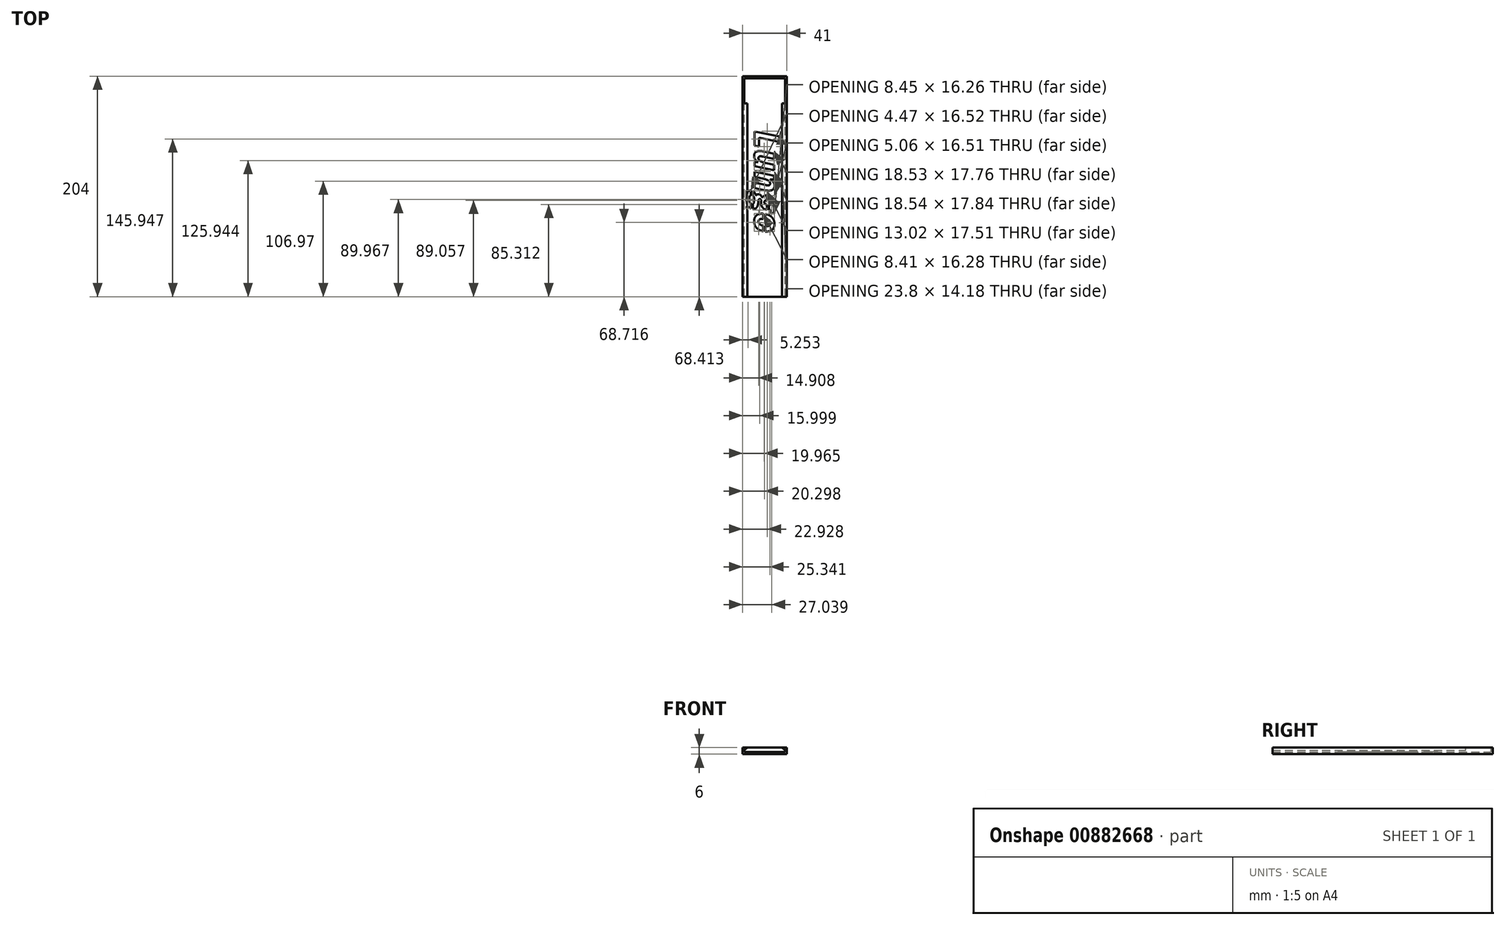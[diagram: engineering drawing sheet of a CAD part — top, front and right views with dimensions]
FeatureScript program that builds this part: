
annotation { "Feature Type Name" : "Feature", "Feature Type Description" : "" }
export const myFeature = defineFeature(function(context is Context, id is Id, definition is map)
    precondition{}
    {
        {
            var Q0;
            Q0=qCreatedBy(makeId("Front.planeOp"),FACE);
            var sketch = newSketch(context, id + "F0", { "sketchPlane" : qUnion([Q0])});
            skLineSegment(sketch, "E0", {"start": v(-20.5, 0) * mm, "end": v(20.5, 0) * mm});
            skLineSegment(sketch, "E1", {"start": v(20.5, 0) * mm, "end": v(20.5, 6) * mm});
            skLineSegment(sketch, "E2", {"start": v(20.5, 6) * mm, "end": v(16, 6) * mm});
            skLineSegment(sketch, "E3", {"start": v(19, 2) * mm, "end": v(-19, 2) * mm});
            skLineSegment(sketch, "E4", {"start": v(-16, 6) * mm, "end": v(-20.5, 6) * mm});
            skLineSegment(sketch, "E5", {"start": v(-20.5, 6) * mm, "end": v(-20.5, 0) * mm});
            skLineSegment(sketch, "E6", {"start": v(-16, 6) * mm, "end": v(16, 6) * mm});
            skLineSegment(sketch, "E7", {"start": v(16, 6) * mm, "end": v(19, 3.6) * mm});
            skLineSegment(sketch, "E8", {"start": v(19, 3.6) * mm, "end": v(19, 2) * mm});
            skLineSegment(sketch, "E9", {"start": v(-16, 6) * mm, "end": v(-19, 3.6) * mm});
            skLineSegment(sketch, "E10", {"start": v(-19, 3.6) * mm, "end": v(-19, 2) * mm});
            skSolve(sketch);
        }
        {
            var Q0;
            Q0=makeQuery(id+"F0.imprint","IMPRINT",FACE,{"disambiguationData":[TD([[makeQuery(id+"F0.imprint","IMPRINT",EDGE,{"derivedFrom":sQuery(id+"F0.wireOp",EDGE,"E0")}),1.0]])]});
            extrude(context, id + "F1", {"entities" : qUnion([Q0]), "depth" : 202 * mm, "offsetDistance" : 25 * mm});
        }
        {
            var Q0;
            Q0=qCreatedBy(makeId("Front.planeOp"),FACE);
            var sketch = newSketch(context, id + "F2", { "sketchPlane" : qUnion([Q0])});
            skLineSegment(sketch, "E11.bottom", {"start": v(20.5, 6) * mm, "end": v(-20.5, 6) * mm});
            skLineSegment(sketch, "E11.top", {"start": v(20.5, 0) * mm, "end": v(-20.5, 0) * mm});
            skLineSegment(sketch, "E11.left", {"start": v(20.5, 6) * mm, "end": v(20.5, 0) * mm});
            skLineSegment(sketch, "E11.right", {"start": v(-20.5, 6) * mm, "end": v(-20.5, 0) * mm});
            skSolve(sketch);
        }
        {
            var Q0;
            Q0=makeQuery(id+"F2.imprint","IMPRINT",FACE,{"disambiguationData":[TD([[makeQuery(id+"F2.imprint","IMPRINT",EDGE,{"derivedFrom":sQuery(id+"F2.wireOp",EDGE,"E11.bottom")}),1.0]])]});
            extrude(context, id + "F3", {"entities" : qUnion([Q0]), "operationType" : NewBodyOperationType.ADD, "oppositeDirection" : true, "depth" : 2 * mm, "offsetDistance" : 25 * mm});
        }
        {
            var Q0;
            Q0=makeQuery(id+"F3.boolean.opBoolean","MERGE",FACE,{"derivedFrom":[makeQuery(id+"F1.opExtrude","SWEPT_FACE",FACE,{"disambiguationData":[OSD([sQuery(id+"F0.wireOp",EDGE,"E2")])]}),makeQuery(id+"F1.opExtrude","SWEPT_FACE",FACE,{"disambiguationData":[OSD([sQuery(id+"F0.wireOp",EDGE,"E4")])]}),makeQuery(id+"F3.opExtrude","SWEPT_FACE",FACE,{"disambiguationData":[OSD([sQuery(id+"F2.wireOp",EDGE,"E11.bottom")])]})]});
            cPlane(context, id + "F4", {"entities" : qUnion([Q0]), "cplaneType" : CPlaneType.OFFSET, "offset" : 0 * mm, "width" : 150 * mm, "height" : 150 * mm});
        }
        {
            var Q0;
            Q0=qCreatedBy(id+"F4.planeOp",FACE);
            var sketch = newSketch(context, id + "F5", { "sketchPlane" : qUnion([Q0])});
            skLineSegment(sketch, "E12.bottom", {"start": v(19, 0) * mm, "end": v(-19, 0) * mm});
            skLineSegment(sketch, "E12.top", {"start": v(19, -23) * mm, "end": v(-19, -23) * mm});
            skLineSegment(sketch, "E12.left", {"start": v(19, 0) * mm, "end": v(19, -23) * mm});
            skLineSegment(sketch, "E12.right", {"start": v(-19, 0) * mm, "end": v(-19, -23) * mm});
            skSolve(sketch);
        }
        {
            var Q0;
            Q0=makeQuery(id+"F5.imprint","IMPRINT",FACE,{"disambiguationData":[TD([[makeQuery(id+"F5.imprint","IMPRINT",EDGE,{"derivedFrom":sQuery(id+"F5.wireOp",EDGE,"E12.bottom")}),1.0]])]});
            extrude(context, id + "F6", {"entities" : qUnion([Q0]), "operationType" : NewBodyOperationType.REMOVE, "oppositeDirection" : true, "depth" : 4 * mm, "offsetDistance" : 25 * mm});
        }
        {
            var Q0;
            Q0=qCreatedBy(id+"F4.planeOp",FACE);
            cPlane(context, id + "F7", {"entities" : qUnion([Q0]), "cplaneType" : CPlaneType.OFFSET, "offset" : 4 * mm, "oppositeDirection" : true, "width" : 150 * mm, "height" : 150 * mm});
        }
        {
            var Q0;
            Q0=qCreatedBy(id+"F7.planeOp",FACE);
            var sketch = newSketch(context, id + "F8", { "sketchPlane" : qUnion([Q0])});
            skText(sketch, "E13", { "text": "Lungo", "fontName": "OpenSans-BoldItalic.ttf"});
            skLineSegment(sketch, "E14.bottom", {"start": v(4.01, -107.75) * mm, "end": v(2.01, -107.75) * mm});
            skLineSegment(sketch, "E14.top", {"start": v(4.01, -122.95) * mm, "end": v(2.01, -122.95) * mm});
            skLineSegment(sketch, "E14.left", {"start": v(4.01, -107.75) * mm, "end": v(4.01, -122.95) * mm});
            skLineSegment(sketch, "E14.right", {"start": v(2.01, -107.75) * mm, "end": v(2.01, -122.95) * mm});
            skLineSegment(sketch, "E15.bottom", {"start": v(0.61, -124.5) * mm, "end": v(-1.39, -124.5) * mm});
            skLineSegment(sketch, "E15.top", {"start": v(0.61, -142.24) * mm, "end": v(-1.39, -142.24) * mm});
            skLineSegment(sketch, "E15.left", {"start": v(0.61, -124.5) * mm, "end": v(0.61, -142.24) * mm});
            skLineSegment(sketch, "E15.right", {"start": v(-1.39, -124.5) * mm, "end": v(-1.39, -142.24) * mm});
            skLineSegment(sketch, "E16.bottom", {"start": v(-11.01, -102.75) * mm, "end": v(-13.01, -102.75) * mm});
            skLineSegment(sketch, "E16.top", {"start": v(-11.01, -124.62) * mm, "end": v(-13.01, -124.62) * mm});
            skLineSegment(sketch, "E16.left", {"start": v(-11.01, -102.75) * mm, "end": v(-11.01, -124.62) * mm});
            skLineSegment(sketch, "E16.right", {"start": v(-13.01, -102.75) * mm, "end": v(-13.01, -124.62) * mm});
            const initialGuessF8  = {"E13": [-0.00947, -0.0481, 0, -1, 0.024]};
            skSetInitialGuess(sketch, initialGuessF8);
            skSolve(sketch);
        }
        {
            var Q0;
            Q0=makeQuery(id+"F8.imprint","IMPRINT",FACE,{"disambiguationData":[TD([[makeQuery(id+"F8.imprint","IMPRINT",EDGE,{"derivedFrom":sQuery(id+"F8.wireOp",EDGE,"E13.sketch_text.stroke-0")}),-1.0]])]});
            var Q1;
            Q1=makeQuery(id+"F8.imprint","IMPRINT",FACE,{"disambiguationData":[TD([[makeQuery(id+"F8.imprint","IMPRINT",EDGE,{"derivedFrom":sQuery(id+"F8.wireOp",EDGE,"E13.sketch_text.stroke-6")}),-1.0]])]});
            var Q2;
            Q2=makeQuery(id+"F8.imprint","IMPRINT",FACE,{"disambiguationData":[TD([[makeQuery(id+"F8.imprint","IMPRINT",EDGE,{"derivedFrom":sQuery(id+"F8.wireOp",EDGE,"E13.sketch_text.stroke-23")}),-1.0]])]});
            var Q3;
            Q3=makeQuery(id+"F8.imprint","IMPRINT",FACE,{"disambiguationData":[TD([[makeQuery(id+"F8.imprint","IMPRINT",EDGE,{"derivedFrom":sQuery(id+"F8.wireOp",EDGE,"E13.sketch_text.stroke-40")}),-1.0]])]});
            var Q4;
            {var subQ17=sQuery(id+"F8.wireOp",EDGE,"E13.sketch_text.stroke-44");Q4=makeQuery(id+"F8.imprint","IMPRINT",FACE,{"disambiguationData":[TD([[makeQuery(id+"F8.imprint","IMPRINT",EDGE,{"derivedFrom":subQ17}),-1.0]])]});}
            var Q5;
            {var subQ9=sQuery(id+"F8.wireOp",EDGE,"E13.sketch_text.stroke-53");Q5=makeQuery(id+"F8.imprint","IMPRINT",FACE,{"disambiguationData":[TD([[makeQuery(id+"F8.imprint","IMPRINT",EDGE,{"derivedFrom":subQ9}),-1.0]])]});}
            var Q6;
            {var subQ7=sQuery(id+"F8.wireOp",EDGE,"E13.sketch_text.stroke-85");Q6=makeQuery(id+"F8.imprint","IMPRINT",FACE,{"disambiguationData":[TD([[makeQuery(id+"F8.imprint","IMPRINT",EDGE,{"derivedFrom":subQ7}),-1.0]])]});}
            var Q7;
            {var subQ5=sQuery(id+"F8.wireOp",EDGE,"E13.sketch_text.stroke-81");Q7=makeQuery(id+"F8.imprint","IMPRINT",FACE,{"disambiguationData":[TD([[makeQuery(id+"F8.imprint","IMPRINT",EDGE,{"derivedFrom":subQ5}),-1.0]])]});}
            var Q8;
            Q8=makeQuery(id+"F3.boolean.opBoolean","MERGE",FACE,{"derivedFrom":[makeQuery(id+"F1.opExtrude","SWEPT_FACE",FACE,{"disambiguationData":[OSD([sQuery(id+"F0.wireOp",EDGE,"E0")])]}),makeQuery(id+"F3.opExtrude","SWEPT_FACE",FACE,{"disambiguationData":[OSD([sQuery(id+"F2.wireOp",EDGE,"E11.top")])]})]});
            extrude(context, id + "F9", {"entities" : qUnion([Q0, Q1, Q2, Q3, Q4, Q5, Q6, Q7]), "operationType" : NewBodyOperationType.REMOVE, "endBound" : BoundingType.UP_TO_SURFACE, "oppositeDirection" : true, "depth" : 25 * mm, "endBoundEntityFace" : qUnion([Q8]), "offsetDistance" : 25 * mm});
        }
    });
